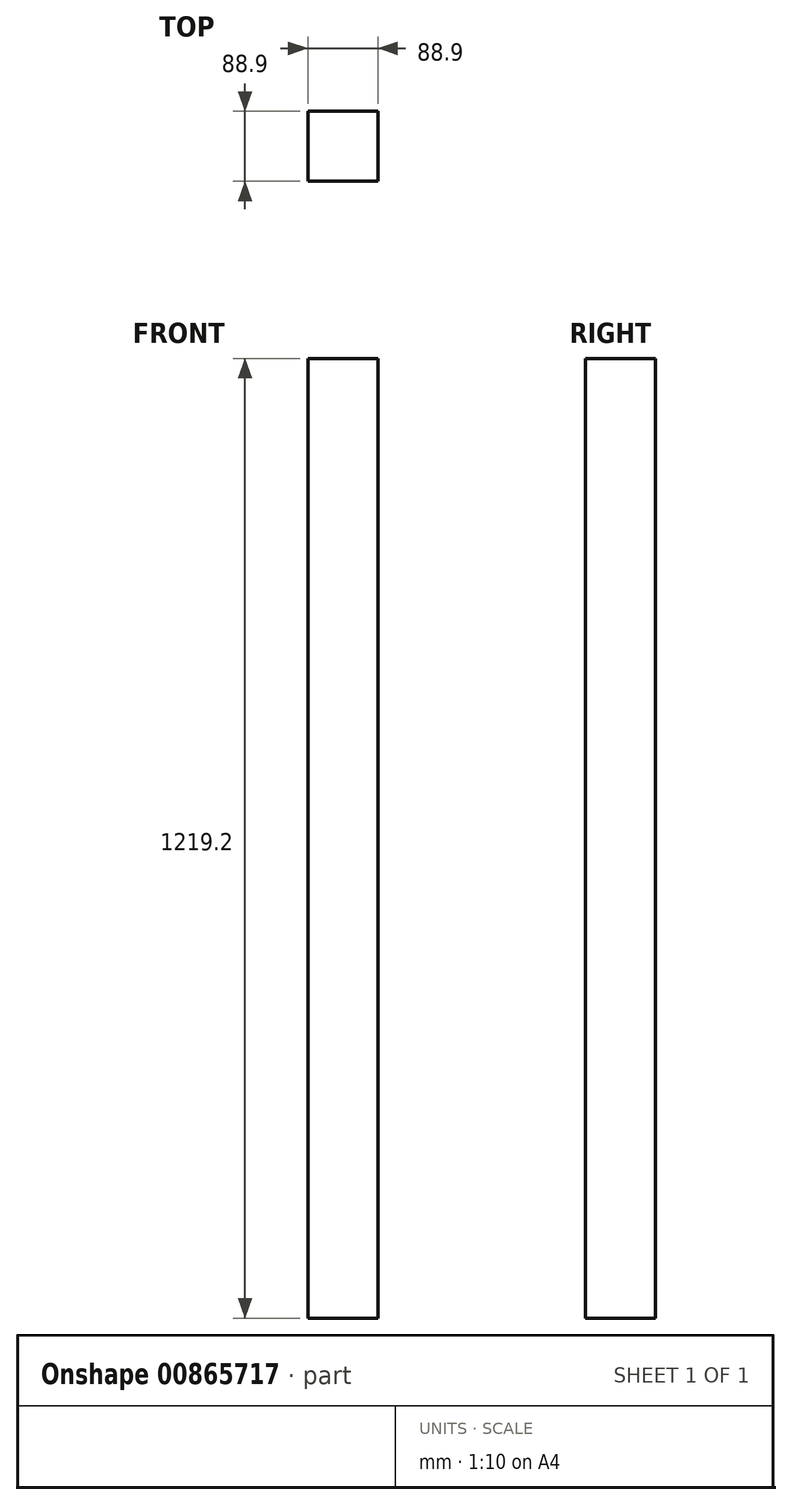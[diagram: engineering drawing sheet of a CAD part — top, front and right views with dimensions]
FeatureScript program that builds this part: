
annotation { "Feature Type Name" : "Feature", "Feature Type Description" : "" }
export const myFeature = defineFeature(function(context is Context, id is Id, definition is map)
    precondition{}
    {
        {
            var Q0;
            Q0=qCreatedBy(makeId("Top.planeOp"),FACE);
            var sketch = newSketch(context, id + "F0", { "sketchPlane" : qUnion([Q0])});
            skLineSegment(sketch, "E0.bottom", {"start": v(0, 0) * mm, "end": v(88.9, 0) * mm});
            skLineSegment(sketch, "E0.top", {"start": v(0, 88.9) * mm, "end": v(88.9, 88.9) * mm});
            skLineSegment(sketch, "E0.left", {"start": v(0, 0) * mm, "end": v(0, 88.9) * mm});
            skLineSegment(sketch, "E0.right", {"start": v(88.9, 0) * mm, "end": v(88.9, 88.9) * mm});
            skSolve(sketch);
        }
        {
            var Q0;
            Q0=makeQuery(id+"F0.imprint","IMPRINT",FACE,{"disambiguationData":[TD([[makeQuery(id+"F0.imprint","IMPRINT",EDGE,{"derivedFrom":sQuery(id+"F0.wireOp",EDGE,"E0.bottom")}),1.0]])]});
            extrude(context, id + "F1", {"entities" : qUnion([Q0]), "depth" : 1219.2 * mm, "offsetDistance" : 25.4 * mm});
        }
    });
